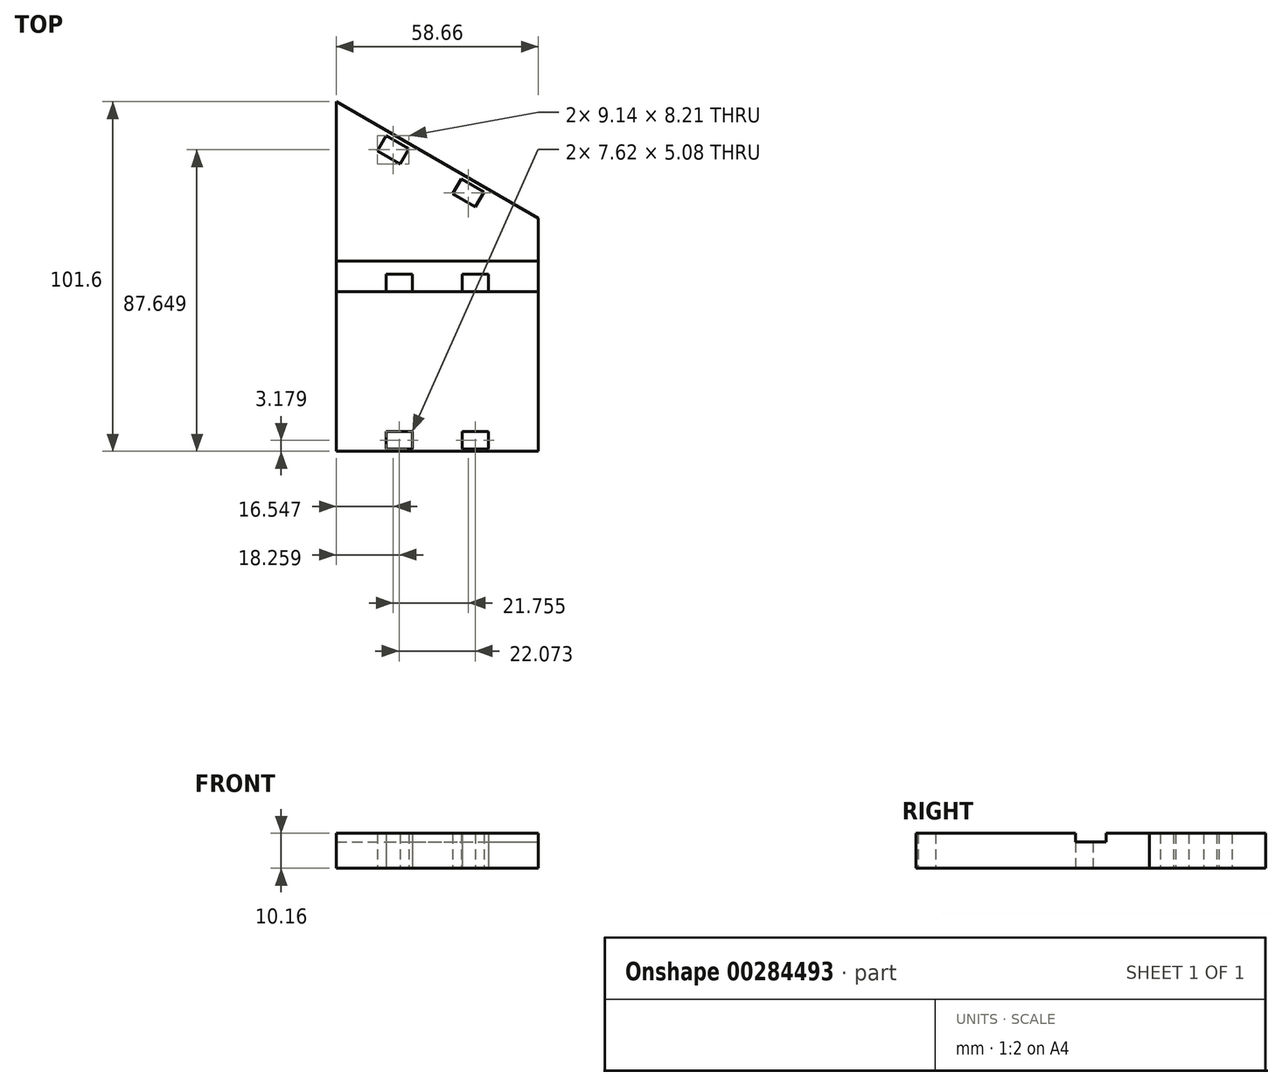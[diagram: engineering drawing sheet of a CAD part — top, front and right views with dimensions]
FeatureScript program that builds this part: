
annotation { "Feature Type Name" : "Feature", "Feature Type Description" : "" }
export const myFeature = defineFeature(function(context is Context, id is Id, definition is map)
    precondition{}
    {
        {
            var Q0;
            Q0=qCreatedBy(makeId("Top.planeOp"),FACE);
            var sketch = newSketch(context, id + "F0", { "sketchPlane" : qUnion([Q0])});
            skLineSegment(sketch, "E0", {"start": v(-23.12, -21.87) * mm, "end": v(-23.12, -123.47) * mm});
            skLineSegment(sketch, "E1", {"start": v(-23.12, -123.47) * mm, "end": v(35.54, -123.47) * mm});
            skLineSegment(sketch, "E2", {"start": v(35.54, -123.47) * mm, "end": v(35.54, -55.73) * mm});
            skLineSegment(sketch, "E3", {"start": v(35.54, -55.73) * mm, "end": v(-23.12, -21.87) * mm});
            skLineSegment(sketch, "E4", {"start": v(-23.12, -117.75) * mm, "end": v(35.54, -117.75) * mm, "construction": true});
            skLineSegment(sketch, "E5.bottom", {"start": v(-8.67, -117.75) * mm, "end": v(-1.05, -117.75) * mm});
            skLineSegment(sketch, "E5.top", {"start": v(-8.67, -122.83) * mm, "end": v(-1.05, -122.83) * mm});
            skLineSegment(sketch, "E5.left", {"start": v(-8.67, -117.75) * mm, "end": v(-8.67, -122.83) * mm});
            skLineSegment(sketch, "E5.right", {"start": v(-1.05, -117.75) * mm, "end": v(-1.05, -122.83) * mm});
            skLineSegment(sketch, "E6.top", {"start": v(8.8, -123.47) * mm, "end": v(25.31, -123.47) * mm});
            skLineSegment(sketch, "E7.bottom", {"start": v(13.4, -117.76) * mm, "end": v(21.02, -117.76) * mm});
            skLineSegment(sketch, "E7.top", {"start": v(13.4, -122.84) * mm, "end": v(21.02, -122.84) * mm});
            skLineSegment(sketch, "E7.left", {"start": v(13.4, -117.76) * mm, "end": v(13.4, -122.84) * mm});
            skLineSegment(sketch, "E7.right", {"start": v(21.02, -117.76) * mm, "end": v(21.02, -122.84) * mm});
            skLineSegment(sketch, "E8", {"start": v(-23.12, -29.2) * mm, "end": v(35.54, -63.07) * mm, "construction": true});
            skLineSegment(sketch, "E9", {"start": v(-8.6, -31.72) * mm, "end": v(-11.14, -36.12) * mm});
            skLineSegment(sketch, "E10", {"start": v(-11.14, -36.12) * mm, "end": v(-4.54, -39.93) * mm});
            skLineSegment(sketch, "E11", {"start": v(-41.2, -53.17) * mm, "end": v(-7.16, 5.78) * mm, "construction": true});
            skLineSegment(sketch, "E12", {"start": v(18.57, -85.12) * mm, "end": v(55.65, -20.89) * mm, "construction": true});
            skLineSegment(sketch, "E13.top", {"start": v(10.61, -48.68) * mm, "end": v(17.21, -52.49) * mm});
            skLineSegment(sketch, "E13.left", {"start": v(13.15, -44.28) * mm, "end": v(10.61, -48.68) * mm});
            skLineSegment(sketch, "E14", {"start": v(-4.54, -39.93) * mm, "end": v(-2, -35.53) * mm});
            skLineSegment(sketch, "E15", {"start": v(-8.6, -31.72) * mm, "end": v(-2, -35.53) * mm});
            skLineSegment(sketch, "E16", {"start": v(17.21, -52.49) * mm, "end": v(19.75, -48.09) * mm});
            skLineSegment(sketch, "E17", {"start": v(13.15, -44.28) * mm, "end": v(19.75, -48.09) * mm});
            skLineSegment(sketch, "E18", {"start": v(-23.12, -68.22) * mm, "end": v(35.54, -68.22) * mm});
            skLineSegment(sketch, "E19", {"start": v(-23.12, -77.11) * mm, "end": v(35.54, -77.11) * mm});
            skLineSegment(sketch, "E20.bottom", {"start": v(-8.67, -72.03) * mm, "end": v(-1.05, -72.03) * mm});
            skLineSegment(sketch, "E20.top", {"start": v(-8.67, -77.11) * mm, "end": v(-1.05, -77.11) * mm});
            skLineSegment(sketch, "E20.left", {"start": v(-8.67, -72.03) * mm, "end": v(-8.67, -77.11) * mm});
            skLineSegment(sketch, "E20.right", {"start": v(-1.05, -72.03) * mm, "end": v(-1.05, -77.11) * mm});
            skLineSegment(sketch, "E21.bottom", {"start": v(13.4, -72.03) * mm, "end": v(21.02, -72.03) * mm});
            skLineSegment(sketch, "E21.top", {"start": v(13.4, -77.11) * mm, "end": v(21.02, -77.11) * mm});
            skLineSegment(sketch, "E21.left", {"start": v(13.4, -72.03) * mm, "end": v(13.4, -77.11) * mm});
            skLineSegment(sketch, "E21.right", {"start": v(21.02, -72.03) * mm, "end": v(21.02, -77.11) * mm});
            skSolve(sketch);
        }
        {
            var Q0;
            {var subQ0=sQuery(id+"F0.wireOp",EDGE,"E3");Q0=makeQuery(id+"F0.imprint","IMPRINT",FACE,{"disambiguationData":[TD([[makeQuery(id+"F0.imprint","IMPRINT",EDGE,{"derivedFrom":subQ0}),1.0]])]});}
            extrude(context, id + "F1", {"entities" : qUnion([Q0]), "depth" : 10.16 * mm});
        }
        {
            var Q0;
            {var subQ0=sQuery(id+"F0.wireOp",EDGE,"E18");Q0=makeQuery(id+"F0.imprint","IMPRINT",FACE,{"disambiguationData":[TD([[makeQuery(id+"F0.imprint","IMPRINT",EDGE,{"derivedFrom":subQ0}),-1.0]])]});}
            extrude(context, id + "F2", {"entities" : qUnion([Q0]), "operationType" : NewBodyOperationType.ADD, "depth" : 7.62 * mm});
        }
        {
            var Q0;
            Q0=makeQuery(id+"F0.imprint","IMPRINT",FACE,{"disambiguationData":[TD([[makeQuery(id+"F0.imprint","IMPRINT",EDGE,{"derivedFrom":sQuery(id+"F0.wireOp",EDGE,"E5.bottom")}),1.0]])]});
            extrude(context, id + "F3", {"entities" : qUnion([Q0]), "operationType" : NewBodyOperationType.ADD, "depth" : 10.16 * mm});
        }
    });
